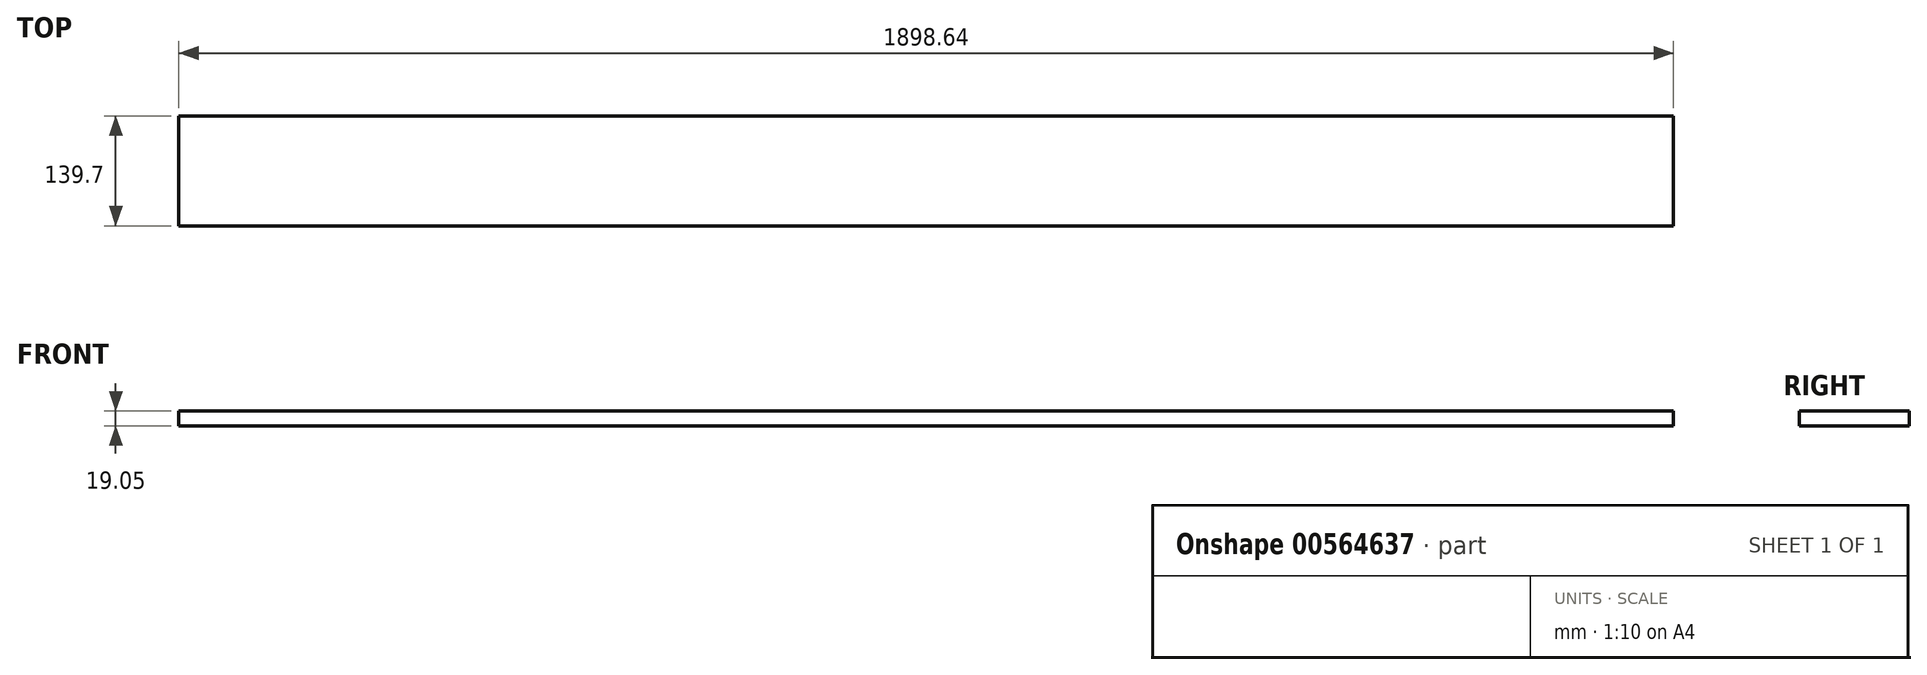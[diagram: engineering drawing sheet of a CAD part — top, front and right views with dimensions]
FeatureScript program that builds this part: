
annotation { "Feature Type Name" : "Feature", "Feature Type Description" : "" }
export const myFeature = defineFeature(function(context is Context, id is Id, definition is map)
    precondition{}
    {
        {
            var Q0;
            Q0=qCreatedBy(makeId("Top.planeOp"),FACE);
            var sketch = newSketch(context, id + "F0", { "sketchPlane" : qUnion([Q0])});
            skLineSegment(sketch, "E0.bottom", {"start": v(-949.33, 69.85) * mm, "end": v(949.33, 69.85) * mm});
            skLineSegment(sketch, "E0.top", {"start": v(-949.33, -69.85) * mm, "end": v(949.33, -69.85) * mm});
            skLineSegment(sketch, "E0.left", {"start": v(-949.33, 69.85) * mm, "end": v(-949.33, -69.85) * mm});
            skLineSegment(sketch, "E0.right", {"start": v(949.33, 69.85) * mm, "end": v(949.33, -69.85) * mm});
            skPoint(sketch, "E0.middle", {"position": v(0, 0) * mm});
            skSolve(sketch);
        }
        {
            var Q0;
            Q0=makeQuery(id+"F0.imprint","IMPRINT",FACE,{"disambiguationData":[TD([[makeQuery(id+"F0.imprint","IMPRINT",EDGE,{"derivedFrom":sQuery(id+"F0.wireOp",EDGE,"E0.bottom")}),-1.0]])]});
            extrude(context, id + "F1", {"entities" : qUnion([Q0]), "depth" : 19.05 * mm, "offsetDistance" : 25.4 * mm});
        }
    });
